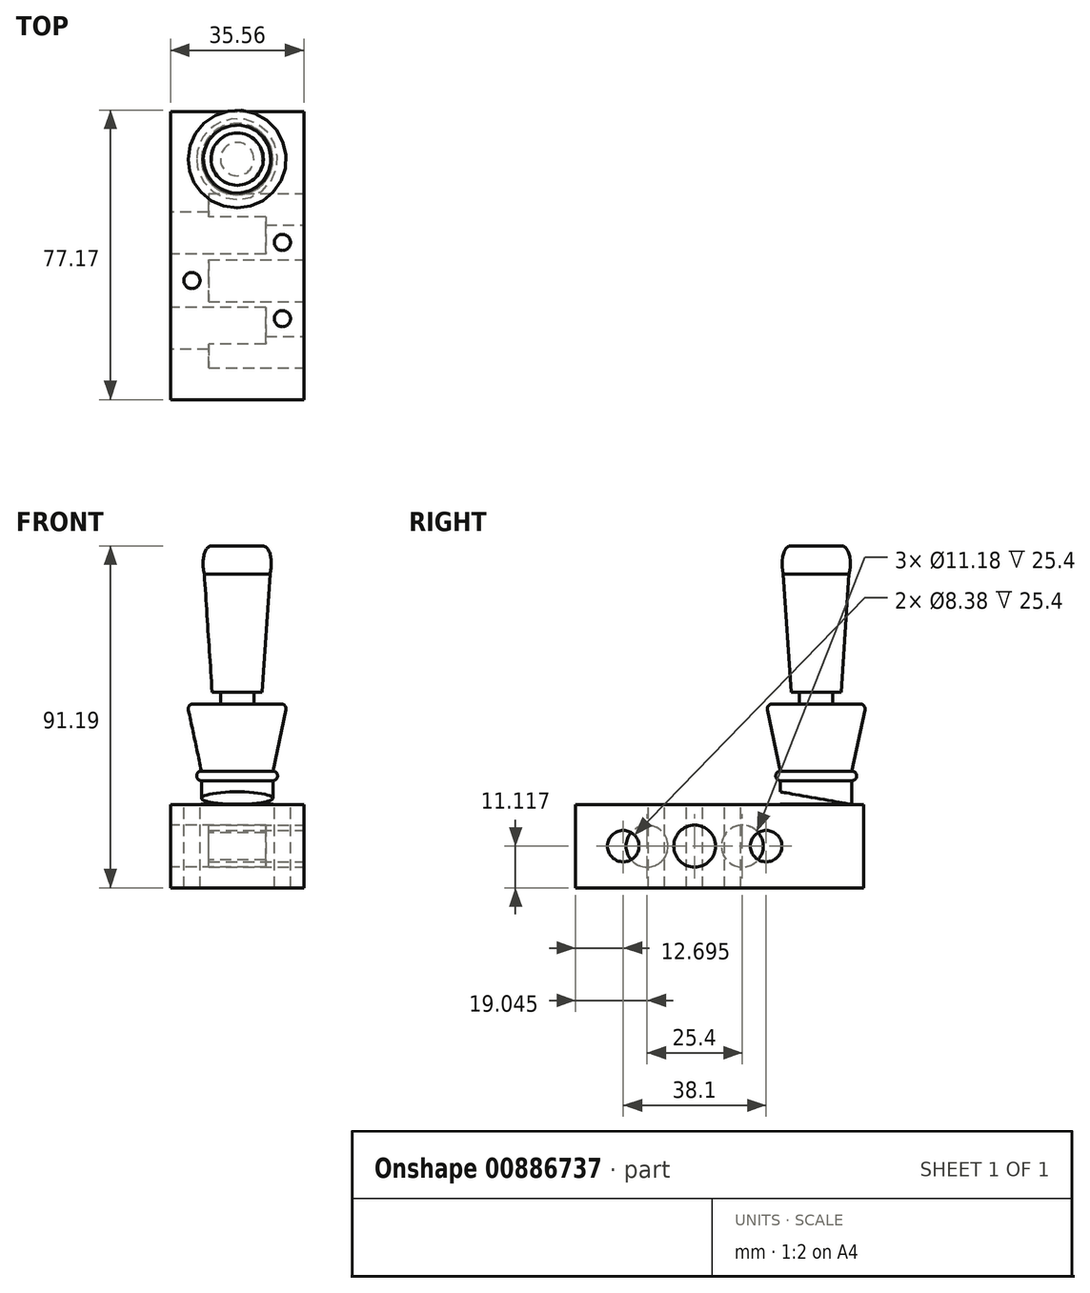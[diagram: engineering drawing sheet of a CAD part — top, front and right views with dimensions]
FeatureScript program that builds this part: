
annotation { "Feature Type Name" : "Feature", "Feature Type Description" : "" }
export const myFeature = defineFeature(function(context is Context, id is Id, definition is map)
    precondition{}
    {
        {
            var Q0;
            Q0=qCreatedBy(makeId("Front.planeOp"),FACE);
            var sketch = newSketch(context, id + "F0", { "sketchPlane" : qUnion([Q0])});
            skLineSegment(sketch, "E0", {"start": v(0, 0) * mm, "end": v(0, 68.96) * mm});
            skLineSegment(sketch, "E1", {"start": v(0, 68.96) * mm, "end": v(6.99, 68.96) * mm});
            skLineSegment(sketch, "E2", {"start": v(9.53, 0) * mm, "end": v(0, 0) * mm});
            skEllipticalArc(sketch, "E3", {});
            skLineSegment(sketch, "E4", {"start": v(6.68, 29.97) * mm, "end": v(8.76, 61.45) * mm});
            skLineSegment(sketch, "E5", {"start": v(6.68, 29.97) * mm, "end": v(4.44, 29.97) * mm});
            skLineSegment(sketch, "E6", {"start": v(4.44, 29.97) * mm, "end": v(4.44, 26.8) * mm});
            skLineSegment(sketch, "E7", {"start": v(4.44, 26.8) * mm, "end": v(11.77, 26.8) * mm});
            skLineSegment(sketch, "E8", {"start": v(9.53, 0) * mm, "end": v(9.53, 6.35) * mm});
            skArc(sketch, "E9", {"start": v(9.53, 6.35) * mm, "mid": v(10.8, 7.62) * mm, "end": v(9.53, 8.9) * mm});
            skLineSegment(sketch, "E10", {"start": v(9.52, 8.89) * mm, "end": v(13, 25.26) * mm});
            skPoint(sketch, "E11.visualSharp", {"position": v(13.33, 26.8) * mm});
            skArc(sketch, "E11.filletArc", {"start": v(13, 25.26) * mm, "mid": v(12.75, 26.33) * mm, "end": v(11.77, 26.8) * mm});
            const initialGuessF0  = {"E3": [0.005514735213005282, 0.06214868913798072, 0.21096714340766978, 0.9774931531230322, 0.006969164786734676, 0.0033230563064474763, 4.71238898038469, 0]};
            skSetInitialGuess(sketch, initialGuessF0);
            skSolve(sketch);
        }
        {
            var Q0;
            Q0 = qSketchRegion(id + "F0", true);
            var Q1;
            Q1=sQuery(id+"F0.wireOp",EDGE,"E0");
            revolve(context, id + "F1", {"surfaceOperationType" : NewSurfaceOperationType.NEW, "entities" : qUnion([Q0]), "axis" : qUnion([Q1]), "revolveType" : RevolveType.FULL});
        }
        {
            var Q0;
            Q0=qCreatedBy(makeId("Top.planeOp"),FACE);
            var sketch = newSketch(context, id + "F2", { "sketchPlane" : qUnion([Q0])});
            skLineSegment(sketch, "E12.bottom", {"start": v(-17.78, 12.7) * mm, "end": v(17.78, 12.7) * mm});
            skLineSegment(sketch, "E12.top", {"start": v(-17.78, -64.13) * mm, "end": v(17.78, -64.13) * mm});
            skLineSegment(sketch, "E12.left", {"start": v(-17.78, 12.7) * mm, "end": v(-17.78, -64.13) * mm});
            skLineSegment(sketch, "E12.right", {"start": v(17.78, 12.7) * mm, "end": v(17.78, -64.13) * mm});
            skSolve(sketch);
        }
        {
            var Q0;
            Q0 = qSketchRegion(id + "F2", true);
            extrude(context, id + "F3", {"entities" : qUnion([Q0]), "oppositeDirection" : true, "depth" : 22.22 * mm, "offsetDistance" : 25.4 * mm});
        }
        {
            var Q0;
            Q0=makeQuery(id+"F3.opExtrude","SWEPT_FACE",FACE,{"disambiguationData":[OSD([sQuery(id+"F2.wireOp",EDGE,"E12.right")])]});
            var sketch = newSketch(context, id + "F4", { "sketchPlane" : qUnion([Q0])});
            skCircle(sketch, "E13", {"center": v(-51.44, -11.11) * mm, "radius": 4.2 * mm});
            skPoint(sketch, "E13.centerSnap0", {"position": v(-64.13, -11.11) * mm});
            skCircle(sketch, "E14", {"center": v(-32.38, -11.11) * mm, "radius": 5.59 * mm});
            skCircle(sketch, "E15", {"center": v(-13.33, -11.11) * mm, "radius": 4.2 * mm});
            skSolve(sketch);
        }
        {
            var Q0;
            Q0=makeQuery(id+"F3.opExtrude","SWEPT_FACE",FACE,{"disambiguationData":[OSD([sQuery(id+"F2.wireOp",EDGE,"E12.left")])]});
            var sketch = newSketch(context, id + "F5", { "sketchPlane" : qUnion([Q0])});
            skCircle(sketch, "E16", {"center": v(45.09, -11.11) * mm, "radius": 5.59 * mm});
            skPoint(sketch, "E16.centerSnap0", {"position": v(64.13, -11.11) * mm});
            skCircle(sketch, "E17", {"center": v(19.68, -11.11) * mm, "radius": 5.59 * mm});
            skSolve(sketch);
        }
        {
            var Q0;
            Q0 = qSketchRegion(id + "F4", true);
            extrude(context, id + "F6", {"entities" : qUnion([Q0]), "operationType" : NewBodyOperationType.REMOVE, "oppositeDirection" : true, "depth" : 25.4 * mm, "offsetDistance" : 25.4 * mm});
        }
        {
            var Q0;
            Q0 = qSketchRegion(id + "F5", true);
            extrude(context, id + "F7", {"entities" : qUnion([Q0]), "operationType" : NewBodyOperationType.REMOVE, "oppositeDirection" : true, "depth" : 25.4 * mm, "offsetDistance" : 25.4 * mm});
        }
        {
            var Q0;
            Q0=qCreatedBy(makeId("Right.planeOp"),FACE);
            var sketch = newSketch(context, id + "F8", { "sketchPlane" : qUnion([Q0])});
            skLineSegment(sketch, "E18.0", {"start": v(9.52, 0) * mm, "end": v(-9.53, 0) * mm});
            skLineSegment(sketch, "E19", {"start": v(-9.53, 0) * mm, "end": v(-9.53, 3.36) * mm});
            skLineSegment(sketch, "E20", {"start": v(9.53, 0) * mm, "end": v(-9.53, 3.36) * mm});
            skPoint(sketch, "E21.orphan", {"position": v(12.7, 0) * mm});
            skPoint(sketch, "E22.orphan", {"position": v(-64.13, 0) * mm});
            skSolve(sketch);
        }
        {
            var Q0;
            Q0 = qSketchRegion(id + "F8", true);
            extrude(context, id + "F9", {"entities" : qUnion([Q0]), "operationType" : NewBodyOperationType.REMOVE, "endBound" : BoundingType.THROUGH_ALL, "oppositeDirection" : true, "depth" : 25.4 * mm, "offsetDistance" : 25.4 * mm, "hasSecondDirection" : true, "secondDirectionBound" : SecondDirectionBoundingType.THROUGH_ALL, "secondDirectionOppositeDirection" : false, "secondDirectionDepth" : 25.4 * mm});
        }
        {
            var Q0;
            Q0=makeQuery(id+"F3.opExtrude","CAP_FACE",FACE,{"disambiguationData":[OSD([sQuery(id+"F2.wireOp",EDGE,"E12.bottom"),sQuery(id+"F2.wireOp",EDGE,"E12.top"),sQuery(id+"F2.wireOp",EDGE,"E12.left"),sQuery(id+"F2.wireOp",EDGE,"E12.right")])],"isStart":true});
            var sketch = newSketch(context, id + "F10", { "sketchPlane" : qUnion([Q0])});
            skCircle(sketch, "E23.0", {"center": v(0, 0) * mm, "radius": 9.53 * mm});
            skSolve(sketch);
        }
        {
            var Q0;
            Q0 = qSketchRegion(id + "F10", true);
            extrude(context, id + "F11", {"entities" : qUnion([Q0]), "operationType" : NewBodyOperationType.ADD, "depth" : 0.13 * mm, "offsetDistance" : 25.4 * mm});
        }
        {
            var Q0;
            Q0=makeQuery(id+"F3.opExtrude","CAP_FACE",FACE,{"disambiguationData":[OSD([sQuery(id+"F2.wireOp",EDGE,"E12.bottom"),sQuery(id+"F2.wireOp",EDGE,"E12.top"),sQuery(id+"F2.wireOp",EDGE,"E12.left"),sQuery(id+"F2.wireOp",EDGE,"E12.right")])],"isStart":true});
            var sketch = newSketch(context, id + "F12", { "sketchPlane" : qUnion([Q0])});
            skCircle(sketch, "E24", {"center": v(-12.07, -32.38) * mm, "radius": 2.16 * mm});
            skCircle(sketch, "E25", {"center": v(12.06, -22.22) * mm, "radius": 2.16 * mm});
            skCircle(sketch, "E26", {"center": v(12.06, -42.55) * mm, "radius": 2.16 * mm});
            skSolve(sketch);
        }
        {
            var Q0;
            Q0 = qSketchRegion(id + "F12", true);
            extrude(context, id + "F13", {"entities" : qUnion([Q0]), "operationType" : NewBodyOperationType.REMOVE, "endBound" : BoundingType.THROUGH_ALL, "oppositeDirection" : true, "depth" : 25.4 * mm, "offsetDistance" : 25.4 * mm});
        }
    });
